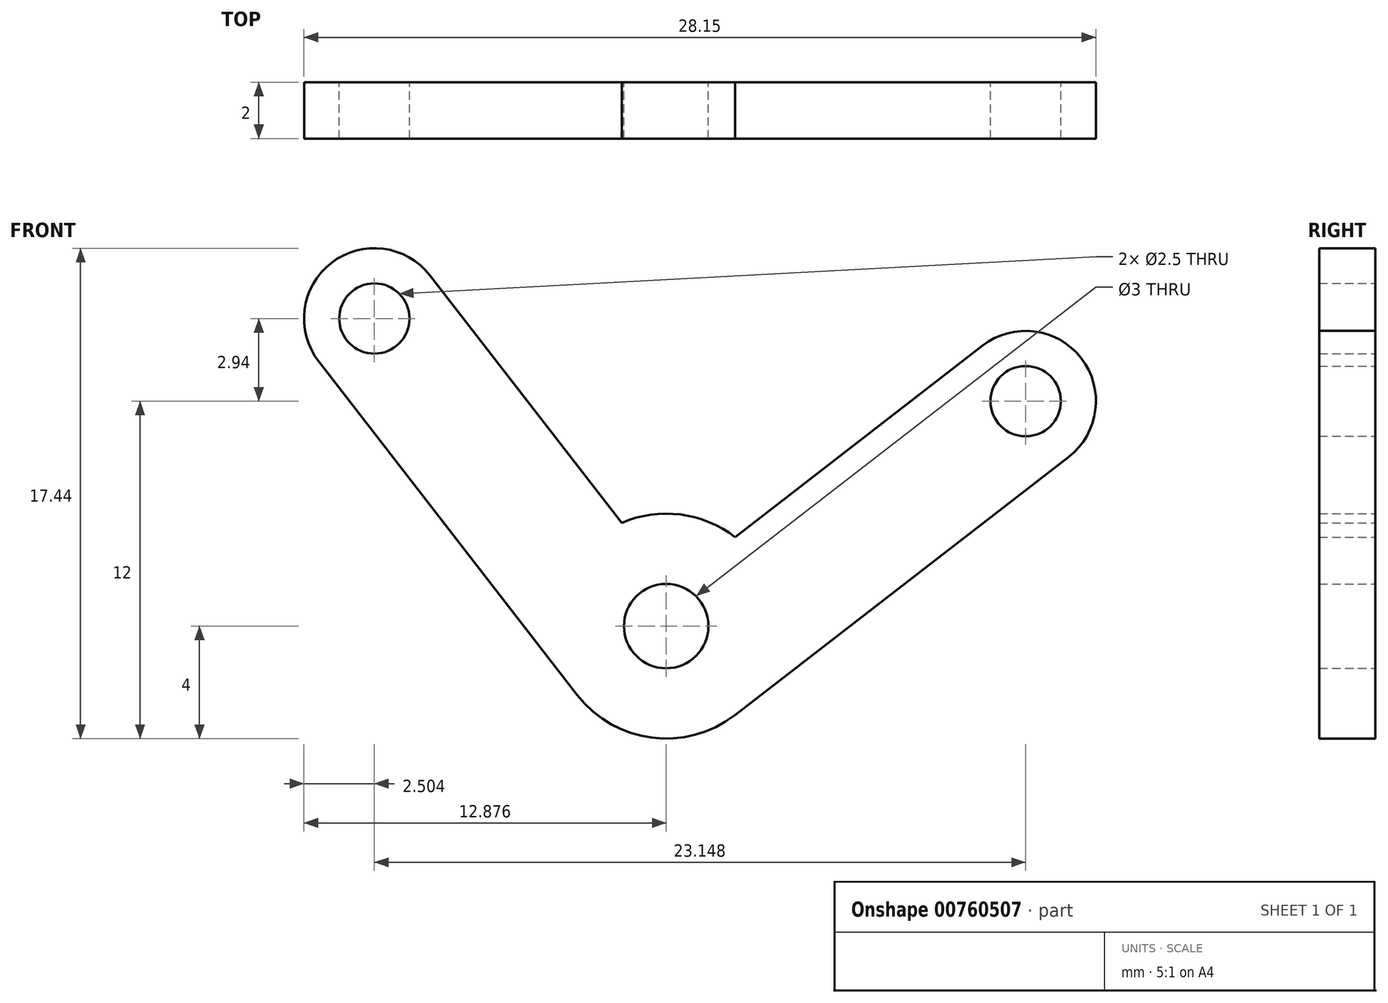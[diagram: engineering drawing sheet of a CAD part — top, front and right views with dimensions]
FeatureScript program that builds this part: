
annotation { "Feature Type Name" : "Feature", "Feature Type Description" : "" }
export const myFeature = defineFeature(function(context is Context, id is Id, definition is map)
    precondition{}
    {
        {
            var Q0;
            Q0=qCreatedBy(makeId("Front.planeOp"),FACE);
            var sketch = newSketch(context, id + "F0", { "sketchPlane" : qUnion([Q0])});
            skCircle(sketch, "E0", {"center": v(9.6, 0) * mm, "radius": 1.5 * mm});
            skArc(sketch, "E1", {"start": v(12.06, 3.16) * mm, "mid": v(10.1, 3.97) * mm, "end": v(8.02, 3.67) * mm});
            skLineSegment(sketch, "E2", {"start": v(6.44, -2.45) * mm, "end": v(-2.74, 9.4) * mm});
            skLineSegment(sketch, "E3", {"start": v(1.21, 12.47) * mm, "end": v(8.02, 3.67) * mm});
            skLineSegment(sketch, "E4", {"start": v(12.06, -3.16) * mm, "end": v(23.91, 6.02) * mm});
            skLineSegment(sketch, "E5", {"start": v(20.85, 9.98) * mm, "end": v(12.06, 3.16) * mm});
            skCircle(sketch, "E6", {"center": v(22.38, 8) * mm, "radius": 1.25 * mm});
            skCircle(sketch, "E7", {"center": v(-0.77, 10.94) * mm, "radius": 1.25 * mm});
            skArc(sketch, "E8", {"start": v(1.21, 12.47) * mm, "mid": v(-2.3, 12.92) * mm, "end": v(-2.74, 9.4) * mm});
            skArc(sketch, "E9", {"start": v(23.91, 6.02) * mm, "mid": v(24.36, 9.53) * mm, "end": v(20.85, 9.98) * mm});
            skArc(sketch, "E10.trimOffspring", {"start": v(6.44, -2.45) * mm, "mid": v(9.1, -3.97) * mm, "end": v(12.06, -3.16) * mm});
            skSolve(sketch);
        }
        {
            var Q0;
            Q0 = qSketchRegion(id + "F0", true);
            extrude(context, id + "F1", {"entities" : qUnion([Q0]), "depth" : 2 * mm, "offsetDistance" : 25 * mm});
        }
    });
